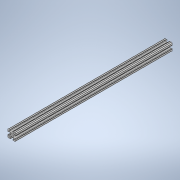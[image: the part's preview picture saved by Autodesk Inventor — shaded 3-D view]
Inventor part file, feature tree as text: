
AUTODESK INVENTOR PART (.ipt)
format: ipt  version: 2020 (Build 240168000, 168)  size: 237,056 bytes
history: native  units: in
note: dims shown in document units (in); Inventor stores cm internally (conversion verified against a paired STEP export)
features: extrude x1, sketch x1
ambient origin geometry x8: Origin, YZ Plane, XZ Plane, XY Plane, X Axis, Y Axis, Z Axis, Center Point
bodies: Solid1 (feature_tree)
feature tree (2):
  extrude  "Extrusion1"  [1 undecoded]
  sketch  "Sketch1"  dims[d0=20.0in d1=0.0in]
note: 1 required parameter value undecoded (feature->parameter linkage not recoverable at this tier; creation-order binding heuristic only, values carry confidence <= 0.55)
